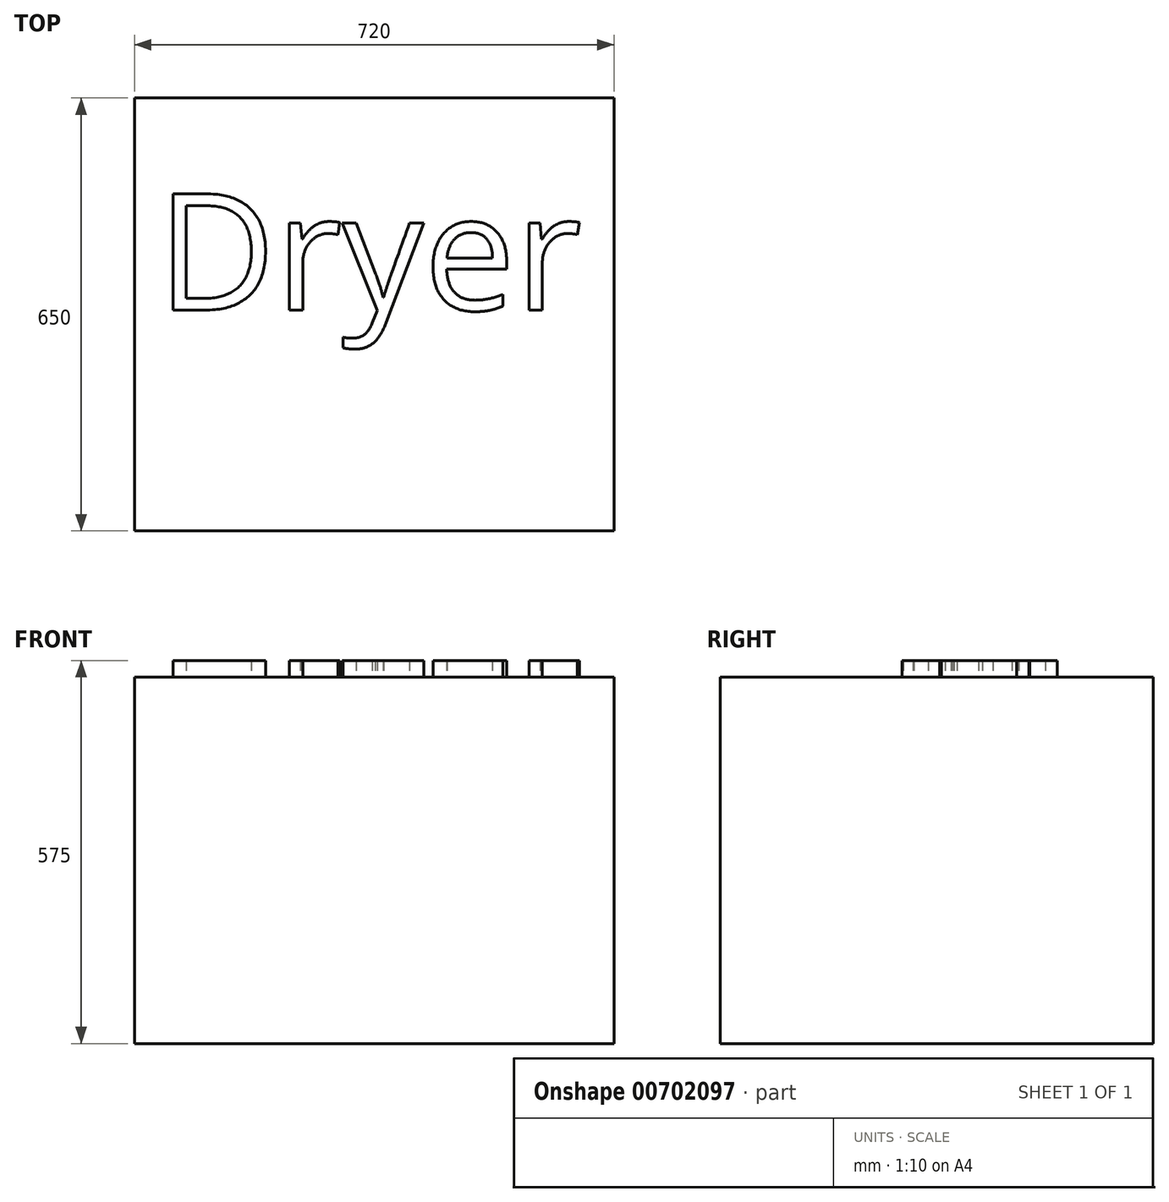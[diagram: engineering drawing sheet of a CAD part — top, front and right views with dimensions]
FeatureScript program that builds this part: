
annotation { "Feature Type Name" : "Feature", "Feature Type Description" : "" }
export const myFeature = defineFeature(function(context is Context, id is Id, definition is map)
    precondition{}
    {
        {
            var Q0;
            Q0=qCreatedBy(makeId("Top.planeOp"),FACE);
            var sketch = newSketch(context, id + "F0", { "sketchPlane" : qUnion([Q0])});
            skLineSegment(sketch, "E0.bottom", {"start": v(0, 0) * mm, "end": v(720, 0) * mm});
            skLineSegment(sketch, "E0.top", {"start": v(0, -650) * mm, "end": v(720, -650) * mm});
            skLineSegment(sketch, "E0.left", {"start": v(0, 0) * mm, "end": v(0, -650) * mm});
            skLineSegment(sketch, "E0.right", {"start": v(720, 0) * mm, "end": v(720, -650) * mm});
            skSolve(sketch);
        }
        {
            var Q0;
            Q0=makeQuery(id+"F0.imprint","IMPRINT",FACE,{"disambiguationData":[TD([[makeQuery(id+"F0.imprint","IMPRINT",EDGE,{"derivedFrom":sQuery(id+"F0.wireOp",EDGE,"E0.bottom")}),-1.0]])]});
            extrude(context, id + "F1", {"entities" : qUnion([Q0]), "depth" : 550 * mm, "offsetDistance" : 25 * mm});
        }
        {
            var Q0;
            Q0=makeQuery(id+"F1.opExtrude","CAP_FACE",FACE,{"disambiguationData":[OSD([sQuery(id+"F0.wireOp",EDGE,"E0.bottom"),sQuery(id+"F0.wireOp",EDGE,"E0.top"),sQuery(id+"F0.wireOp",EDGE,"E0.left"),sQuery(id+"F0.wireOp",EDGE,"E0.right")])],"isStart":false});
            var sketch = newSketch(context, id + "F2", { "sketchPlane" : qUnion([Q0])});
            skText(sketch, "E1", { "text": "Dryer", "fontName": "OpenSans-Regular.ttf"});
            const initialGuessF2  = {"E1": [0.03375, -0.31853, 1, 0, 0.17586]};
            skSetInitialGuess(sketch, initialGuessF2);
            skSolve(sketch);
        }
        {
            var Q0;
            Q0 = qSketchRegion(id + "F2", true);
            extrude(context, id + "F3", {"entities" : qUnion([Q0]), "operationType" : NewBodyOperationType.ADD, "depth" : 25 * mm, "offsetDistance" : 25 * mm});
        }
    });
